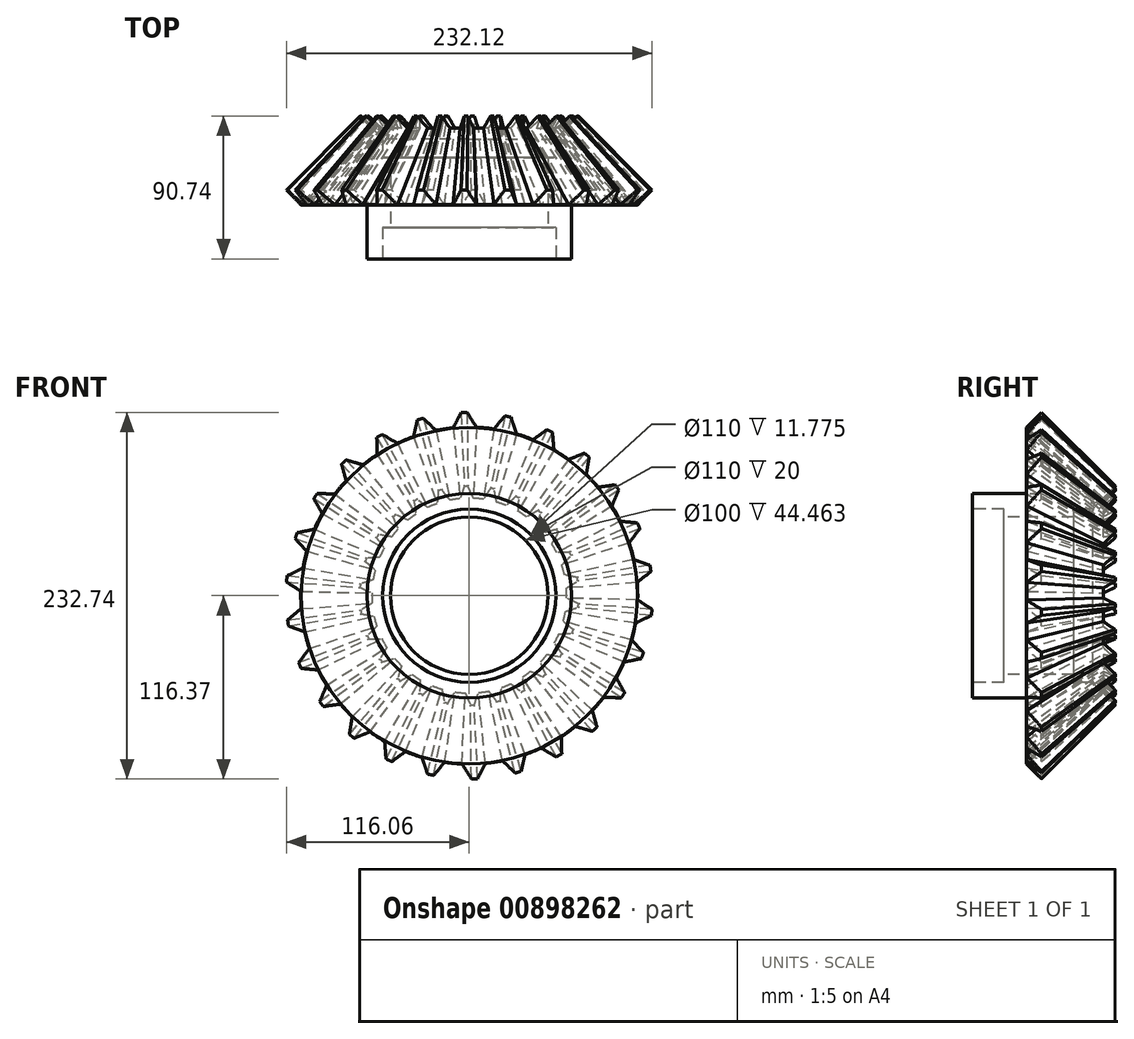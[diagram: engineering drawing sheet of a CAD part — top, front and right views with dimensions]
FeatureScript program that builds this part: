
annotation { "Feature Type Name" : "Feature", "Feature Type Description" : "" }
export const myFeature = defineFeature(function(context is Context, id is Id, definition is map)
    precondition{}
    {
        {
            var Q0;
            Q0=qCreatedBy(makeId("Front.planeOp"),FACE);
            var sketch = newSketch(context, id + "F0", { "sketchPlane" : qUnion([Q0])});
            skArc(sketch, "E0", {"start": v(-1.47, 126) * mm, "mid": v(-3.63, 125.95) * mm, "end": v(-5.8, 125.87) * mm});
            skArc(sketch, "E1", {"start": v(-35.45, 101.22) * mm, "mid": v(-40.62, 99.26) * mm, "end": v(-45.68, 97.04) * mm});
            skLineSegment(sketch, "E2", {"start": v(-5.8, 125.87) * mm, "end": v(-10.2, 106.76) * mm});
            skLineSegment(sketch, "E3", {"start": v(-1.47, 126) * mm, "end": v(4.65, 107.15) * mm});
            skLineSegment(sketch, "E4", {"start": v(-35.75, 120.82) * mm, "end": v(-35.45, 101.22) * mm});
            skArc(sketch, "E5", {"start": v(-31.58, 121.98) * mm, "mid": v(-33.67, 121.42) * mm, "end": v(-35.75, 120.82) * mm});
            skLineSegment(sketch, "E6", {"start": v(-31.58, 121.98) * mm, "end": v(-21.13, 105.15) * mm});
            skLineSegment(sketch, "E7", {"start": v(-63.63, 108.76) * mm, "end": v(-58.64, 89.8) * mm});
            skArc(sketch, "E8", {"start": v(-59.85, 110.88) * mm, "mid": v(-61.75, 109.83) * mm, "end": v(-63.63, 108.76) * mm});
            skLineSegment(sketch, "E9", {"start": v(-59.85, 110.88) * mm, "end": v(-45.68, 97.04) * mm});
            skLineSegment(sketch, "E10", {"start": v(-87.8, 90.37) * mm, "end": v(-78.43, 73.15) * mm});
            skArc(sketch, "E11", {"start": v(-84.65, 93.33) * mm, "mid": v(-86.24, 91.86) * mm, "end": v(-87.8, 90.37) * mm});
            skLineSegment(sketch, "E12", {"start": v(-84.65, 93.33) * mm, "end": v(-67.57, 83.28) * mm});
            skLineSegment(sketch, "E13", {"start": v(-106.88, 66.73) * mm, "end": v(-93.66, 52.26) * mm});
            skArc(sketch, "E14", {"start": v(-104.52, 70.36) * mm, "mid": v(-105.72, 68.56) * mm, "end": v(-106.88, 66.73) * mm});
            skLineSegment(sketch, "E15", {"start": v(-104.52, 70.36) * mm, "end": v(-85.54, 64.7) * mm});
            skLineSegment(sketch, "E16", {"start": v(-119.74, 39.21) * mm, "end": v(-103.44, 28.33) * mm});
            skArc(sketch, "E17", {"start": v(-118.33, 43.3) * mm, "mid": v(-119.05, 41.26) * mm, "end": v(-119.74, 39.21) * mm});
            skLineSegment(sketch, "E18", {"start": v(-118.33, 43.3) * mm, "end": v(-98.54, 42.34) * mm});
            skLineSegment(sketch, "E19", {"start": v(-125.65, 9.42) * mm, "end": v(-107.21, 2.75) * mm});
            skArc(sketch, "E20", {"start": v(-125.25, 13.73) * mm, "mid": v(-125.47, 11.57) * mm, "end": v(-125.65, 9.42) * mm});
            skLineSegment(sketch, "E21", {"start": v(-125.25, 13.73) * mm, "end": v(-105.8, 17.53) * mm});
            skLineSegment(sketch, "E22", {"start": v(-124.25, -20.93) * mm, "end": v(-104.76, -23) * mm});
            skArc(sketch, "E23", {"start": v(-124.9, -16.65) * mm, "mid": v(-124.6, -18.79) * mm, "end": v(-124.25, -20.93) * mm});
            skLineSegment(sketch, "E24", {"start": v(-124.9, -16.65) * mm, "end": v(-106.93, -8.3) * mm});
            skLineSegment(sketch, "E25", {"start": v(-115.63, -50.05) * mm, "end": v(-96.21, -47.4) * mm});
            skArc(sketch, "E26", {"start": v(-117.28, -46.05) * mm, "mid": v(-116.47, -48.06) * mm, "end": v(-115.63, -50.05) * mm});
            skLineSegment(sketch, "E27", {"start": v(-117.28, -46.05) * mm, "end": v(-101.83, -33.65) * mm});
            skLineSegment(sketch, "E28", {"start": v(-100.3, -76.27) * mm, "end": v(-82.07, -69.04) * mm});
            skArc(sketch, "E29", {"start": v(-102.85, -72.78) * mm, "mid": v(-101.59, -74.54) * mm, "end": v(-100.3, -76.27) * mm});
            skLineSegment(sketch, "E30", {"start": v(-102.85, -72.78) * mm, "end": v(-90.82, -57.04) * mm});
            skLineSegment(sketch, "E31", {"start": v(-79.13, -98.06) * mm, "end": v(-63.17, -86.68) * mm});
            skArc(sketch, "E32", {"start": v(-82.45, -95.28) * mm, "mid": v(-80.8, -96.68) * mm, "end": v(-79.13, -98.06) * mm});
            skLineSegment(sketch, "E33", {"start": v(-82.45, -95.28) * mm, "end": v(-74.53, -77.12) * mm});
            skLineSegment(sketch, "E34", {"start": v(-53.36, -114.14) * mm, "end": v(-40.59, -99.27) * mm});
            skArc(sketch, "E35", {"start": v(-57.25, -112.24) * mm, "mid": v(-55.31, -113.2) * mm, "end": v(-53.36, -114.14) * mm});
            skLineSegment(sketch, "E36", {"start": v(-57.25, -112.24) * mm, "end": v(-53.9, -92.72) * mm});
            skLineSegment(sketch, "E37", {"start": v(-24.5, -123.6) * mm, "end": v(-15.65, -106.1) * mm});
            skArc(sketch, "E38", {"start": v(-28.72, -122.68) * mm, "mid": v(-26.61, -123.16) * mm, "end": v(-24.5, -123.6) * mm});
            skLineSegment(sketch, "E39", {"start": v(-28.72, -122.68) * mm, "end": v(-30.15, -102.92) * mm});
            skLineSegment(sketch, "E40", {"start": v(5.8, -125.87) * mm, "end": v(10.2, -106.76) * mm});
            skArc(sketch, "E41", {"start": v(1.47, -126) * mm, "mid": v(3.63, -125.95) * mm, "end": v(5.8, -125.87) * mm});
            skLineSegment(sketch, "E42", {"start": v(1.47, -126) * mm, "end": v(-4.65, -107.15) * mm});
            skLineSegment(sketch, "E43", {"start": v(35.75, -120.82) * mm, "end": v(35.45, -101.22) * mm});
            skArc(sketch, "E44", {"start": v(31.58, -121.98) * mm, "mid": v(33.67, -121.42) * mm, "end": v(35.75, -120.82) * mm});
            skLineSegment(sketch, "E45", {"start": v(31.58, -121.98) * mm, "end": v(21.13, -105.15) * mm});
            skLineSegment(sketch, "E46", {"start": v(63.63, -108.76) * mm, "end": v(58.64, -89.8) * mm});
            skArc(sketch, "E47", {"start": v(59.85, -110.88) * mm, "mid": v(61.75, -109.83) * mm, "end": v(63.63, -108.76) * mm});
            skLineSegment(sketch, "E48", {"start": v(59.85, -110.88) * mm, "end": v(45.68, -97.04) * mm});
            skLineSegment(sketch, "E49", {"start": v(87.8, -90.37) * mm, "end": v(78.43, -73.15) * mm});
            skArc(sketch, "E50", {"start": v(84.65, -93.33) * mm, "mid": v(86.24, -91.86) * mm, "end": v(87.8, -90.37) * mm});
            skLineSegment(sketch, "E51", {"start": v(84.65, -93.33) * mm, "end": v(67.57, -83.28) * mm});
            skLineSegment(sketch, "E52", {"start": v(106.88, -66.73) * mm, "end": v(93.66, -52.26) * mm});
            skArc(sketch, "E53", {"start": v(104.52, -70.36) * mm, "mid": v(105.72, -68.56) * mm, "end": v(106.88, -66.73) * mm});
            skLineSegment(sketch, "E54", {"start": v(104.52, -70.36) * mm, "end": v(85.54, -64.7) * mm});
            skLineSegment(sketch, "E55", {"start": v(119.74, -39.21) * mm, "end": v(103.44, -28.33) * mm});
            skArc(sketch, "E56", {"start": v(118.33, -43.3) * mm, "mid": v(119.05, -41.26) * mm, "end": v(119.74, -39.21) * mm});
            skLineSegment(sketch, "E57", {"start": v(118.33, -43.3) * mm, "end": v(98.54, -42.34) * mm});
            skLineSegment(sketch, "E58", {"start": v(125.65, -9.42) * mm, "end": v(107.21, -2.75) * mm});
            skArc(sketch, "E59", {"start": v(125.25, -13.73) * mm, "mid": v(125.47, -11.57) * mm, "end": v(125.65, -9.42) * mm});
            skLineSegment(sketch, "E60", {"start": v(125.25, -13.73) * mm, "end": v(105.8, -17.53) * mm});
            skLineSegment(sketch, "E61", {"start": v(124.25, 20.93) * mm, "end": v(104.76, 23) * mm});
            skArc(sketch, "E62", {"start": v(124.9, 16.65) * mm, "mid": v(124.6, 18.79) * mm, "end": v(124.25, 20.93) * mm});
            skLineSegment(sketch, "E63", {"start": v(124.9, 16.65) * mm, "end": v(106.93, 8.3) * mm});
            skLineSegment(sketch, "E64", {"start": v(115.63, 50.05) * mm, "end": v(96.21, 47.4) * mm});
            skArc(sketch, "E65", {"start": v(117.28, 46.05) * mm, "mid": v(116.47, 48.06) * mm, "end": v(115.63, 50.05) * mm});
            skLineSegment(sketch, "E66", {"start": v(117.28, 46.05) * mm, "end": v(101.83, 33.65) * mm});
            skLineSegment(sketch, "E67", {"start": v(100.3, 76.27) * mm, "end": v(82.07, 69.04) * mm});
            skArc(sketch, "E68", {"start": v(102.85, 72.78) * mm, "mid": v(101.59, 74.54) * mm, "end": v(100.3, 76.27) * mm});
            skLineSegment(sketch, "E69", {"start": v(102.85, 72.78) * mm, "end": v(90.82, 57.04) * mm});
            skLineSegment(sketch, "E70", {"start": v(79.13, 98.06) * mm, "end": v(63.17, 86.68) * mm});
            skArc(sketch, "E71", {"start": v(82.45, 95.28) * mm, "mid": v(80.8, 96.68) * mm, "end": v(79.13, 98.06) * mm});
            skLineSegment(sketch, "E72", {"start": v(82.45, 95.28) * mm, "end": v(74.53, 77.12) * mm});
            skLineSegment(sketch, "E73", {"start": v(53.36, 114.14) * mm, "end": v(40.59, 99.27) * mm});
            skArc(sketch, "E74", {"start": v(57.25, 112.24) * mm, "mid": v(55.31, 113.2) * mm, "end": v(53.36, 114.14) * mm});
            skLineSegment(sketch, "E75", {"start": v(57.25, 112.24) * mm, "end": v(53.9, 92.72) * mm});
            skLineSegment(sketch, "E76", {"start": v(24.5, 123.6) * mm, "end": v(15.65, 106.1) * mm});
            skArc(sketch, "E77", {"start": v(28.72, 122.68) * mm, "mid": v(26.61, 123.16) * mm, "end": v(24.5, 123.6) * mm});
            skLineSegment(sketch, "E78", {"start": v(28.72, 122.68) * mm, "end": v(30.15, 102.92) * mm});
            skArc(sketch, "E79", {"start": v(-58.64, 89.8) * mm, "mid": v(-63.2, 86.66) * mm, "end": v(-67.57, 83.28) * mm});
            skArc(sketch, "E80", {"start": v(-78.43, 73.15) * mm, "mid": v(-82.1, 69.01) * mm, "end": v(-85.54, 64.7) * mm});
            skArc(sketch, "E81", {"start": v(-93.66, 52.26) * mm, "mid": v(-96.23, 47.36) * mm, "end": v(-98.54, 42.34) * mm});
            skArc(sketch, "E82", {"start": v(-103.44, 28.33) * mm, "mid": v(-104.76, 22.96) * mm, "end": v(-105.8, 17.53) * mm});
            skArc(sketch, "E83", {"start": v(-107.21, 2.75) * mm, "mid": v(-107.21, -2.78) * mm, "end": v(-106.93, -8.3) * mm});
            skArc(sketch, "E84", {"start": v(-104.76, -23) * mm, "mid": v(-103.43, -28.36) * mm, "end": v(-101.83, -33.65) * mm});
            skArc(sketch, "E85", {"start": v(-96.21, -47.4) * mm, "mid": v(-93.64, -52.29) * mm, "end": v(-90.82, -57.04) * mm});
            skArc(sketch, "E86", {"start": v(-82.07, -69.04) * mm, "mid": v(-78.4, -73.18) * mm, "end": v(-74.53, -77.12) * mm});
            skArc(sketch, "E87", {"start": v(-63.17, -86.68) * mm, "mid": v(-58.62, -89.82) * mm, "end": v(-53.9, -92.72) * mm});
            skArc(sketch, "E88", {"start": v(-40.59, -99.27) * mm, "mid": v(-35.42, -101.23) * mm, "end": v(-30.15, -102.92) * mm});
            skArc(sketch, "E89", {"start": v(-15.65, -106.1) * mm, "mid": v(-10.16, -106.77) * mm, "end": v(-4.65, -107.15) * mm});
            skArc(sketch, "E90", {"start": v(10.2, -106.76) * mm, "mid": v(15.68, -106.1) * mm, "end": v(21.13, -105.15) * mm});
            skArc(sketch, "E91", {"start": v(35.45, -101.22) * mm, "mid": v(40.62, -99.26) * mm, "end": v(45.68, -97.04) * mm});
            skArc(sketch, "E92", {"start": v(58.64, -89.8) * mm, "mid": v(63.2, -86.66) * mm, "end": v(67.57, -83.28) * mm});
            skArc(sketch, "E93", {"start": v(78.43, -73.15) * mm, "mid": v(82.1, -69.01) * mm, "end": v(85.54, -64.7) * mm});
            skArc(sketch, "E94", {"start": v(93.66, -52.26) * mm, "mid": v(96.23, -47.36) * mm, "end": v(98.54, -42.34) * mm});
            skArc(sketch, "E95", {"start": v(103.44, -28.33) * mm, "mid": v(104.76, -22.96) * mm, "end": v(105.8, -17.53) * mm});
            skArc(sketch, "E96", {"start": v(107.21, -2.75) * mm, "mid": v(107.21, 2.78) * mm, "end": v(106.93, 8.3) * mm});
            skArc(sketch, "E97", {"start": v(104.76, 23) * mm, "mid": v(103.43, 28.36) * mm, "end": v(101.83, 33.65) * mm});
            skArc(sketch, "E98", {"start": v(96.21, 47.4) * mm, "mid": v(93.64, 52.29) * mm, "end": v(90.82, 57.04) * mm});
            skArc(sketch, "E99", {"start": v(82.07, 69.04) * mm, "mid": v(78.4, 73.18) * mm, "end": v(74.53, 77.12) * mm});
            skArc(sketch, "E100", {"start": v(63.17, 86.68) * mm, "mid": v(58.62, 89.82) * mm, "end": v(53.9, 92.72) * mm});
            skArc(sketch, "E101", {"start": v(40.59, 99.27) * mm, "mid": v(35.42, 101.23) * mm, "end": v(30.15, 102.92) * mm});
            skArc(sketch, "E102", {"start": v(15.65, 106.1) * mm, "mid": v(10.16, 106.77) * mm, "end": v(4.65, 107.15) * mm});
            skArc(sketch, "E103", {"start": v(-10.2, 106.76) * mm, "mid": v(-15.68, 106.1) * mm, "end": v(-21.13, 105.15) * mm});
            skSolve(sketch);
        }
        {
            var Q0;
            Q0=makeQuery(id+"F0.imprint","IMPRINT",FACE,{"disambiguationData":[TD([[makeQuery(id+"F0.imprint","IMPRINT",EDGE,{"derivedFrom":sQuery(id+"F0.wireOp",EDGE,"E0")}),1.0]])]});
            cPlane(context, id + "F1", {"entities" : qUnion([Q0]), "cplaneType" : CPlaneType.OFFSET, "offset" : 56.57 * mm, "oppositeDirection" : true, "width" : 150 * mm, "height" : 150 * mm});
        }
        {
            var Q0;
            Q0=qCreatedBy(id+"F1.planeOp",FACE);
            var sketch = newSketch(context, id + "F2", { "sketchPlane" : qUnion([Q0])});
            skPoint(sketch, "E104.0", {"position": v(0, 0) * mm});
            skArc(sketch, "E105", {"start": v(-18.1, 51.66) * mm, "mid": v(-20.73, 50.66) * mm, "end": v(-23.31, 49.52) * mm});
            skArc(sketch, "E106", {"start": v(-0.8, 69.43) * mm, "mid": v(-2, 69.4) * mm, "end": v(-3.2, 69.36) * mm});
            skLineSegment(sketch, "E107", {"start": v(2.37, 54.68) * mm, "end": v(-0.8, 69.43) * mm});
            skLineSegment(sketch, "E108", {"start": v(-3.2, 69.36) * mm, "end": v(-5.2, 54.49) * mm});
            skArc(sketch, "E109.1.0", {"start": v(-17.4, 67.22) * mm, "mid": v(-18.55, 66.9) * mm, "end": v(-19.7, 66.58) * mm});
            skLineSegment(sketch, "E109.1.1", {"start": v(-19.7, 66.58) * mm, "end": v(-18.1, 51.66) * mm});
            skLineSegment(sketch, "E109.1.2", {"start": v(-10.78, 53.66) * mm, "end": v(-17.4, 67.22) * mm});
            skArc(sketch, "E109.2.0", {"start": v(-32.98, 61.1) * mm, "mid": v(-34.03, 60.52) * mm, "end": v(-35.06, 59.93) * mm});
            skLineSegment(sketch, "E109.2.1", {"start": v(-35.06, 59.93) * mm, "end": v(-29.93, 45.83) * mm});
            skLineSegment(sketch, "E109.2.2", {"start": v(-23.31, 49.52) * mm, "end": v(-32.98, 61.1) * mm});
            skArc(sketch, "E109.3.0", {"start": v(-46.64, 51.43) * mm, "mid": v(-47.52, 50.62) * mm, "end": v(-48.38, 49.8) * mm});
            skLineSegment(sketch, "E109.3.1", {"start": v(-48.38, 49.8) * mm, "end": v(-40.03, 37.33) * mm});
            skLineSegment(sketch, "E109.3.2", {"start": v(-34.49, 42.5) * mm, "end": v(-46.64, 51.43) * mm});
            skArc(sketch, "E109.4.0", {"start": v(-57.6, 38.77) * mm, "mid": v(-58.25, 37.78) * mm, "end": v(-58.9, 36.77) * mm});
            skLineSegment(sketch, "E109.4.1", {"start": v(-58.9, 36.77) * mm, "end": v(-47.8, 26.67) * mm});
            skLineSegment(sketch, "E109.4.2", {"start": v(-43.65, 33.01) * mm, "end": v(-57.6, 38.77) * mm});
            skArc(sketch, "E109.5.0", {"start": v(-65.2, 23.86) * mm, "mid": v(-65.6, 22.74) * mm, "end": v(-65.98, 21.6) * mm});
            skLineSegment(sketch, "E109.5.1", {"start": v(-65.98, 21.6) * mm, "end": v(-52.79, 14.46) * mm});
            skLineSegment(sketch, "E109.5.2", {"start": v(-50.29, 21.6) * mm, "end": v(-65.2, 23.86) * mm});
            skArc(sketch, "E109.6.0", {"start": v(-69.02, 7.56) * mm, "mid": v(-69.14, 6.38) * mm, "end": v(-69.24, 5.19) * mm});
            skLineSegment(sketch, "E109.6.1", {"start": v(-69.24, 5.19) * mm, "end": v(-54.72, 1.4) * mm});
            skLineSegment(sketch, "E109.6.2", {"start": v(-54, 8.95) * mm, "end": v(-69.02, 7.56) * mm});
            skArc(sketch, "E109.7.0", {"start": v(-68.82, -9.17) * mm, "mid": v(-68.66, -10.35) * mm, "end": v(-68.47, -11.53) * mm});
            skLineSegment(sketch, "E109.7.1", {"start": v(-68.47, -11.53) * mm, "end": v(-53.46, -11.73) * mm});
            skLineSegment(sketch, "E109.7.2", {"start": v(-54.57, -4.24) * mm, "end": v(-68.82, -9.17) * mm});
            skArc(sketch, "E109.8.0", {"start": v(-64.63, -25.38) * mm, "mid": v(-64.18, -26.48) * mm, "end": v(-63.72, -27.58) * mm});
            skLineSegment(sketch, "E109.8.1", {"start": v(-63.72, -27.58) * mm, "end": v(-49.1, -24.19) * mm});
            skLineSegment(sketch, "E109.8.2", {"start": v(-51.97, -17.17) * mm, "end": v(-64.63, -25.38) * mm});
            skArc(sketch, "E109.9.0", {"start": v(-56.68, -40.1) * mm, "mid": v(-55.98, -41.07) * mm, "end": v(-55.27, -42.03) * mm});
            skLineSegment(sketch, "E109.9.1", {"start": v(-55.27, -42.03) * mm, "end": v(-41.88, -35.23) * mm});
            skLineSegment(sketch, "E109.9.2", {"start": v(-46.35, -29.11) * mm, "end": v(-56.68, -40.1) * mm});
            skArc(sketch, "E109.10.0", {"start": v(-45.43, -52.5) * mm, "mid": v(-44.52, -53.28) * mm, "end": v(-43.6, -54.03) * mm});
            skLineSegment(sketch, "E109.10.1", {"start": v(-43.6, -54.03) * mm, "end": v(-32.24, -44.23) * mm});
            skLineSegment(sketch, "E109.10.2", {"start": v(-38.04, -39.36) * mm, "end": v(-45.43, -52.5) * mm});
            skArc(sketch, "E109.11.0", {"start": v(-31.55, -61.85) * mm, "mid": v(-30.48, -62.38) * mm, "end": v(-29.4, -62.9) * mm});
            skLineSegment(sketch, "E109.11.1", {"start": v(-29.4, -62.9) * mm, "end": v(-20.71, -50.66) * mm});
            skLineSegment(sketch, "E109.11.2", {"start": v(-27.51, -47.32) * mm, "end": v(-31.55, -61.85) * mm});
            skArc(sketch, "E109.12.0", {"start": v(-15.83, -67.6) * mm, "mid": v(-14.66, -67.87) * mm, "end": v(-13.5, -68.1) * mm});
            skLineSegment(sketch, "E109.12.1", {"start": v(-13.5, -68.1) * mm, "end": v(-7.99, -54.15) * mm});
            skLineSegment(sketch, "E109.12.2", {"start": v(-15.39, -52.53) * mm, "end": v(-15.83, -67.6) * mm});
            skArc(sketch, "E109.13.0", {"start": v(0.8, -69.43) * mm, "mid": v(2, -69.4) * mm, "end": v(3.2, -69.36) * mm});
            skLineSegment(sketch, "E109.13.1", {"start": v(3.2, -69.36) * mm, "end": v(5.2, -54.49) * mm});
            skLineSegment(sketch, "E109.13.2", {"start": v(-2.37, -54.68) * mm, "end": v(0.8, -69.43) * mm});
            skArc(sketch, "E109.14.0", {"start": v(17.4, -67.22) * mm, "mid": v(18.55, -66.9) * mm, "end": v(19.7, -66.58) * mm});
            skLineSegment(sketch, "E109.14.1", {"start": v(19.7, -66.58) * mm, "end": v(18.1, -51.66) * mm});
            skLineSegment(sketch, "E109.14.2", {"start": v(10.78, -53.66) * mm, "end": v(17.4, -67.22) * mm});
            skArc(sketch, "E109.15.0", {"start": v(32.98, -61.1) * mm, "mid": v(34.03, -60.52) * mm, "end": v(35.06, -59.93) * mm});
            skLineSegment(sketch, "E109.15.1", {"start": v(35.06, -59.93) * mm, "end": v(29.93, -45.83) * mm});
            skLineSegment(sketch, "E109.15.2", {"start": v(23.31, -49.52) * mm, "end": v(32.98, -61.1) * mm});
            skArc(sketch, "E109.16.0", {"start": v(46.64, -51.43) * mm, "mid": v(47.52, -50.62) * mm, "end": v(48.38, -49.8) * mm});
            skLineSegment(sketch, "E109.16.1", {"start": v(48.38, -49.8) * mm, "end": v(40.03, -37.33) * mm});
            skLineSegment(sketch, "E109.16.2", {"start": v(34.49, -42.5) * mm, "end": v(46.64, -51.43) * mm});
            skArc(sketch, "E109.17.0", {"start": v(57.6, -38.77) * mm, "mid": v(58.25, -37.78) * mm, "end": v(58.9, -36.77) * mm});
            skLineSegment(sketch, "E109.17.1", {"start": v(58.9, -36.77) * mm, "end": v(47.8, -26.67) * mm});
            skLineSegment(sketch, "E109.17.2", {"start": v(43.65, -33.01) * mm, "end": v(57.6, -38.77) * mm});
            skArc(sketch, "E109.18.0", {"start": v(65.2, -23.86) * mm, "mid": v(65.6, -22.74) * mm, "end": v(65.98, -21.6) * mm});
            skLineSegment(sketch, "E109.18.1", {"start": v(65.98, -21.6) * mm, "end": v(52.79, -14.46) * mm});
            skLineSegment(sketch, "E109.18.2", {"start": v(50.29, -21.6) * mm, "end": v(65.2, -23.86) * mm});
            skArc(sketch, "E109.19.0", {"start": v(69.02, -7.56) * mm, "mid": v(69.14, -6.38) * mm, "end": v(69.24, -5.19) * mm});
            skLineSegment(sketch, "E109.19.1", {"start": v(69.24, -5.19) * mm, "end": v(54.72, -1.4) * mm});
            skLineSegment(sketch, "E109.19.2", {"start": v(54, -8.95) * mm, "end": v(69.02, -7.56) * mm});
            skArc(sketch, "E109.20.0", {"start": v(68.82, 9.17) * mm, "mid": v(68.66, 10.35) * mm, "end": v(68.47, 11.53) * mm});
            skLineSegment(sketch, "E109.20.1", {"start": v(68.47, 11.53) * mm, "end": v(53.46, 11.73) * mm});
            skLineSegment(sketch, "E109.20.2", {"start": v(54.57, 4.24) * mm, "end": v(68.82, 9.17) * mm});
            skArc(sketch, "E109.21.0", {"start": v(64.63, 25.38) * mm, "mid": v(64.18, 26.48) * mm, "end": v(63.72, 27.58) * mm});
            skLineSegment(sketch, "E109.21.1", {"start": v(63.72, 27.58) * mm, "end": v(49.1, 24.19) * mm});
            skLineSegment(sketch, "E109.21.2", {"start": v(51.97, 17.17) * mm, "end": v(64.63, 25.38) * mm});
            skArc(sketch, "E109.22.0", {"start": v(56.68, 40.1) * mm, "mid": v(55.98, 41.07) * mm, "end": v(55.27, 42.03) * mm});
            skLineSegment(sketch, "E109.22.1", {"start": v(55.27, 42.03) * mm, "end": v(41.88, 35.23) * mm});
            skLineSegment(sketch, "E109.22.2", {"start": v(46.35, 29.11) * mm, "end": v(56.68, 40.1) * mm});
            skArc(sketch, "E109.23.0", {"start": v(45.43, 52.5) * mm, "mid": v(44.52, 53.28) * mm, "end": v(43.6, 54.03) * mm});
            skLineSegment(sketch, "E109.23.1", {"start": v(43.6, 54.03) * mm, "end": v(32.24, 44.23) * mm});
            skLineSegment(sketch, "E109.23.2", {"start": v(38.04, 39.36) * mm, "end": v(45.43, 52.5) * mm});
            skArc(sketch, "E109.24.0", {"start": v(31.55, 61.85) * mm, "mid": v(30.48, 62.38) * mm, "end": v(29.4, 62.9) * mm});
            skLineSegment(sketch, "E109.24.1", {"start": v(29.4, 62.9) * mm, "end": v(20.71, 50.66) * mm});
            skLineSegment(sketch, "E109.24.2", {"start": v(27.51, 47.32) * mm, "end": v(31.55, 61.85) * mm});
            skArc(sketch, "E109.25.0", {"start": v(15.83, 67.6) * mm, "mid": v(14.66, 67.87) * mm, "end": v(13.5, 68.1) * mm});
            skLineSegment(sketch, "E109.25.1", {"start": v(13.5, 68.1) * mm, "end": v(7.99, 54.15) * mm});
            skLineSegment(sketch, "E109.25.2", {"start": v(15.39, 52.53) * mm, "end": v(15.83, 67.6) * mm});
            skArc(sketch, "E110.trimOffspring", {"start": v(-29.93, 45.83) * mm, "mid": v(-32.25, 44.22) * mm, "end": v(-34.49, 42.5) * mm});
            skArc(sketch, "E111.trimOffspring", {"start": v(-40.03, 37.33) * mm, "mid": v(-41.9, 35.22) * mm, "end": v(-43.65, 33.01) * mm});
            skArc(sketch, "E112.trimOffspring", {"start": v(-47.8, 26.67) * mm, "mid": v(-49.1, 24.17) * mm, "end": v(-50.29, 21.6) * mm});
            skArc(sketch, "E113.trimOffspring", {"start": v(-52.79, 14.46) * mm, "mid": v(-53.46, 11.72) * mm, "end": v(-54, 8.95) * mm});
            skArc(sketch, "E114.trimOffspring", {"start": v(-54.72, 1.4) * mm, "mid": v(-54.71, -1.42) * mm, "end": v(-54.57, -4.24) * mm});
            skArc(sketch, "E115.trimOffspring", {"start": v(-53.46, -11.73) * mm, "mid": v(-52.79, -14.47) * mm, "end": v(-51.97, -17.17) * mm});
            skArc(sketch, "E116.trimOffspring", {"start": v(-49.1, -24.19) * mm, "mid": v(-47.79, -26.68) * mm, "end": v(-46.35, -29.11) * mm});
            skArc(sketch, "E117.trimOffspring", {"start": v(-5.2, 54.49) * mm, "mid": v(-8, 54.14) * mm, "end": v(-10.78, 53.66) * mm});
            skArc(sketch, "E118.trimOffspring", {"start": v(7.99, 54.15) * mm, "mid": v(5.19, 54.49) * mm, "end": v(2.37, 54.68) * mm});
            skArc(sketch, "E119.trimOffspring", {"start": v(20.71, 50.66) * mm, "mid": v(18.07, 51.66) * mm, "end": v(15.39, 52.53) * mm});
            skArc(sketch, "E120.trimOffspring", {"start": v(32.24, 44.23) * mm, "mid": v(29.91, 45.84) * mm, "end": v(27.51, 47.32) * mm});
            skArc(sketch, "E121.trimOffspring", {"start": v(41.88, 35.23) * mm, "mid": v(40.01, 37.34) * mm, "end": v(38.04, 39.36) * mm});
            skArc(sketch, "E122.trimOffspring", {"start": v(49.1, 24.19) * mm, "mid": v(47.79, 26.68) * mm, "end": v(46.35, 29.11) * mm});
            skArc(sketch, "E123.trimOffspring", {"start": v(53.46, 11.73) * mm, "mid": v(52.79, 14.47) * mm, "end": v(51.97, 17.17) * mm});
            skArc(sketch, "E124.trimOffspring", {"start": v(54.72, -1.4) * mm, "mid": v(54.71, 1.42) * mm, "end": v(54.57, 4.24) * mm});
            skArc(sketch, "E125.trimOffspring", {"start": v(52.79, -14.46) * mm, "mid": v(53.46, -11.72) * mm, "end": v(54, -8.95) * mm});
            skArc(sketch, "E126.trimOffspring", {"start": v(47.8, -26.67) * mm, "mid": v(49.1, -24.17) * mm, "end": v(50.29, -21.6) * mm});
            skArc(sketch, "E127.trimOffspring", {"start": v(40.03, -37.33) * mm, "mid": v(41.9, -35.22) * mm, "end": v(43.65, -33.01) * mm});
            skArc(sketch, "E128.trimOffspring", {"start": v(29.93, -45.83) * mm, "mid": v(32.25, -44.22) * mm, "end": v(34.49, -42.5) * mm});
            skArc(sketch, "E129.trimOffspring", {"start": v(18.1, -51.66) * mm, "mid": v(20.73, -50.66) * mm, "end": v(23.31, -49.52) * mm});
            skArc(sketch, "E130.trimOffspring", {"start": v(5.2, -54.49) * mm, "mid": v(8, -54.14) * mm, "end": v(10.78, -53.66) * mm});
            skArc(sketch, "E131.trimOffspring", {"start": v(-7.99, -54.15) * mm, "mid": v(-5.19, -54.49) * mm, "end": v(-2.37, -54.68) * mm});
            skArc(sketch, "E132.trimOffspring", {"start": v(-20.71, -50.66) * mm, "mid": v(-18.07, -51.66) * mm, "end": v(-15.39, -52.53) * mm});
            skArc(sketch, "E133.trimOffspring", {"start": v(-32.24, -44.23) * mm, "mid": v(-29.91, -45.84) * mm, "end": v(-27.51, -47.32) * mm});
            skArc(sketch, "E134.trimOffspring", {"start": v(-41.88, -35.23) * mm, "mid": v(-40.01, -37.34) * mm, "end": v(-38.04, -39.36) * mm});
            skSolve(sketch);
        }
        {
            var Q0;
            Q0=makeQuery(id+"F0.imprint","IMPRINT",FACE,{"disambiguationData":[TD([[makeQuery(id+"F0.imprint","IMPRINT",EDGE,{"derivedFrom":sQuery(id+"F0.wireOp",EDGE,"E0")}),1.0]])]});
            var Q1;
            Q1=makeQuery(id+"F2.imprint","IMPRINT",FACE,{"disambiguationData":[TD([[makeQuery(id+"F2.imprint","IMPRINT",EDGE,{"derivedFrom":sQuery(id+"F2.wireOp",EDGE,"E105")}),1.0]])]});
            loft(context, id + "F3", {"sheetProfilesArray" : [{ "sheetProfileEntities" : qUnion([Q0]) }, { "sheetProfileEntities" : qUnion([Q1]) }]});
        }
        {
            var Q0;
            Q0=makeQuery(id+"F3.opLoft","CAP_FACE",FACE,{"disambiguationData":[OSD([makeQuery(id+"F0.imprint","IMPRINT",FACE,{"disambiguationData":[TD([[makeQuery(id+"F0.imprint","IMPRINT",EDGE,{"derivedFrom":sQuery(id+"F0.wireOp",EDGE,"E0")}),1.0]])]})])],"isStart":true});
            var sketch = newSketch(context, id + "F4", { "sketchPlane" : qUnion([Q0])});
            skCircle(sketch, "E135", {"center": v(0, 0) * mm, "radius": 65 * mm});
            skSolve(sketch);
        }
        {
            var Q0;
            Q0=makeQuery(id+"F4.imprint","IMPRINT",FACE,{"disambiguationData":[TD([[makeQuery(id+"F4.imprint","IMPRINT",EDGE,{"derivedFrom":sQuery(id+"F4.wireOp",EDGE,"E135")}),1.0]])]});
            extrude(context, id + "F5", {"entities" : qUnion([Q0]), "operationType" : NewBodyOperationType.ADD, "depth" : 34.25 * mm, "offsetDistance" : 25 * mm});
        }
        {
            var Q0;
            Q0=makeQuery(id+"F5.opExtrude","CAP_FACE",FACE,{"disambiguationData":[OSD([sQuery(id+"F4.wireOp",EDGE,"E135")])],"isStart":false});
            var sketch = newSketch(context, id + "F6", { "sketchPlane" : qUnion([Q0])});
            skCircle(sketch, "E136", {"center": v(0, 0) * mm, "radius": 50 * mm});
            skCircle(sketch, "E137", {"center": v(0, 0) * mm, "radius": 55 * mm});
            skSolve(sketch);
        }
        {
            var Q0;
            Q0=makeQuery(id+"F6.imprint","IMPRINT",FACE,{"disambiguationData":[TD([[makeQuery(id+"F6.imprint","IMPRINT",EDGE,{"derivedFrom":sQuery(id+"F6.wireOp",EDGE,"E136")}),-1.0]])]});
            extrude(context, id + "F7", {"entities" : qUnion([Q0]), "operationType" : NewBodyOperationType.REMOVE, "oppositeDirection" : true, "depth" : 20 * mm, "offsetDistance" : 25 * mm});
        }
        {
            var Q0;
            Q0=makeQuery(id+"F7.boolean.opBoolean","COPY",FACE,{"derivedFrom":makeQuery(id+"F7.opExtrude","CAP_FACE",FACE,{"disambiguationData":[OSD([sQuery(id+"F6.wireOp",EDGE,"E136"),sQuery(id+"F6.wireOp",EDGE,"E137")])],"isStart":false})});
            cPlane(context, id + "F8", {"entities" : qUnion([Q0]), "cplaneType" : CPlaneType.OFFSET, "offset" : 44.46 * mm, "oppositeDirection" : true, "width" : 150 * mm, "height" : 150 * mm});
        }
        {
            var Q0;
            Q0=qCreatedBy(id+"F8.planeOp",FACE);
            var sketch = newSketch(context, id + "F9", { "sketchPlane" : qUnion([Q0])});
            skCircle(sketch, "E138.0", {"center": v(0, 0) * mm, "radius": 55 * mm});
            skCircle(sketch, "E139.0", {"center": v(0, 0) * mm, "radius": 50 * mm});
            skSolve(sketch);
        }
        {
            var Q0;
            Q0 = qSketchRegion(id + "F9", true);
            extrude(context, id + "F10", {"entities" : qUnion([Q0]), "operationType" : NewBodyOperationType.REMOVE, "oppositeDirection" : true, "depth" : 73 * mm, "offsetDistance" : 25 * mm});
        }
        {
            var Q0;
            Q0=makeQuery(id+"F7.boolean.opBoolean","SPLIT",FACE,{"disambiguationData":[TD([makeQuery(id+"F7.opExtrude","SWEPT_FACE",FACE,{"disambiguationData":[OSD([sQuery(id+"F6.wireOp",EDGE,"E136")])]})])],"derivedFrom":makeQuery(id+"F5.opExtrude","CAP_FACE",FACE,{"disambiguationData":[OSD([sQuery(id+"F4.wireOp",EDGE,"E135")])],"isStart":false})});
            extrude(context, id + "F11", {"entities" : qUnion([Q0]), "operationType" : NewBodyOperationType.REMOVE, "oppositeDirection" : true, "depth" : 333 * mm, "offsetDistance" : 25 * mm});
        }
        {
            var Q0;
            Q0=qCreatedBy(makeId("Right.planeOp"),FACE);
            var sketch = newSketch(context, id + "F12", { "sketchPlane" : qUnion([Q0])});
            skPoint(sketch, "E140.0", {"position": v(0, 106.76) * mm});
            skLineSegment(sketch, "E141", {"start": v(0, 106.76) * mm, "end": v(22.67, 129.43) * mm});
            skLineSegment(sketch, "E142", {"start": v(22.67, 129.43) * mm, "end": v(0, 129.43) * mm});
            skLineSegment(sketch, "E143", {"start": v(0, 129.43) * mm, "end": v(0, 106.76) * mm});
            skPoint(sketch, "E144.0", {"position": v(56.57, 54.76) * mm});
            skLineSegment(sketch, "E145", {"start": v(56.64, 69.66) * mm, "end": v(41.74, 54.76) * mm});
            skLineSegment(sketch, "E146", {"start": v(41.74, 54.76) * mm, "end": v(56.64, 54.76) * mm});
            skLineSegment(sketch, "E147", {"start": v(56.64, 54.76) * mm, "end": v(56.64, 69.66) * mm});
            skPoint(sketch, "E148.0", {"position": v(56.57, 69.43) * mm});
            skSolve(sketch);
        }
        {
            var Q0;
            Q0=makeQuery(id+"F12.imprint","IMPRINT",FACE,{"disambiguationData":[TD([[makeQuery(id+"F12.imprint","IMPRINT",EDGE,{"derivedFrom":sQuery(id+"F12.wireOp",EDGE,"E145")}),1.0]])]});
            var Q1;
            Q1=makeQuery(id+"F12.imprint","IMPRINT",FACE,{"disambiguationData":[TD([[makeQuery(id+"F12.imprint","IMPRINT",EDGE,{"derivedFrom":sQuery(id+"F12.wireOp",EDGE,"E141")}),1.0]])]});
            var Q2;
            Q2=makeQuery(id+"F5.opExtrude","CAP_EDGE",EDGE,{"disambiguationData":[OSD([sQuery(id+"F4.wireOp",EDGE,"E135")])],"isStart":false});
            revolve(context, id + "F13", {"operationType" : NewBodyOperationType.REMOVE, "surfaceOperationType" : NewSurfaceOperationType.NEW, "entities" : qUnion([Q0, Q1]), "axis" : qUnion([Q2]), "revolveType" : RevolveType.FULL, "oppositeDirection" : true});
        }
    });
